# Revit family: leddownlightrc-sl-e_rd150-12w-4000-wh_140056558
name_source: partatom
category: Leuchten
revit_build: Autodesk Revit 2016 (Build: 20190508_0715(x64)
units: mm (PartAtom-declared; Revit-internal decimal feet)

## family parameters
Basisbauteil = Fläche
Beim Laden mit Abzugskörper schneiden = Nein
Bemaßung runder Anschluss = Durchmesser verwenden
Gemeinsam genutzt = Nein
Lichtquelle = Nein
Raumberechnungspunkt = Nein
Teiletyp = Normal

## types (1)
- LEDDownlightRc-Sl-E Rd150-12W-4000-WH (1 x LED, 1050 lm)
    Approval mark = CE
    Beschreibung = Slim LED Downlight. Very flat design, only 34mm height. Integrated driver for easier installation. Suitable for retrofitting due to available adapter ring sizes. IP44 on light emitting side.
    CIE Flux Codes = 47 78 95 100 100
    Control Gear = Electronic ballast
    Height = 0 mm  [stored 0 ft]
    Hersteller = OPPLE
    Lamp Light Flux = 1050 lm
    Lamp count = 1
    Lampe = 1 x LED
    Length = 163 mm
    Luminous efficacy = 88 lm/W
    ModVariant = Nein
    Modell = 140056558
    Mounting Place = Ceiling
    Mounting Type = Recessed
    Number of Poles = 1
    OnlyDefault = Ja
    Power Factor = 1
    Product Name = LEDDownlightRc-Sl-E Rd150-12W-4000-WH
    Product group = Downlight Slim EcoMax
    ProductGroupID = 405
    Protection Class = Protection class II
    Protection Degree = IP 44
    RLX_Detail_Level = 1
    RlxData = <blob elided: 154669 chars, md5=1033c76f>
    Scheinlast = 12 VA
    Socket = socket
    Standby Power = 0 W
    System Light Flux = 1050 lm
    System Power = 12 W
    Typenbild = 140056558.jpg
    Typenkommentare = Product without accessories
    URL = http://relux.com
    VarID = ---
    Voltage = 0 V
    Vorgabe-Ansicht = 1800 mm
    Weight = 0.00 kg
    Width = 0 mm  [stored 0 ft]

note: [stored X ft] marks values corroborated as IEEE doubles in the binary element streams (Revit-internal decimal feet)

## geometry (parser evidence)
native form markers: Blend x4, Sweep x9
no freeform markers — native parametric forms only
